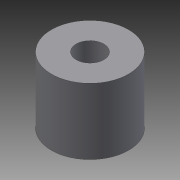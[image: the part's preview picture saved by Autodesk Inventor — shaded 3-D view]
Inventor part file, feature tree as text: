
AUTODESK INVENTOR PART (.ipt)
format: ipt  version: 2014 (Build 180170000, 170)  size: 73,216 bytes
history: native  units: mm
features: other x1, extrude x1, sketch x1
ambient origin geometry x8: Origin, YZ Plane, XZ Plane, XY Plane, X Axis, Y Axis, Z Axis, Center Point
bodies: Body1 (feature_tree)
feature tree (3):
  other  "Твердое тело1"
  extrude  "Выдавливание1"  Depth=2.5mm
  sketch  "Эскиз1"
